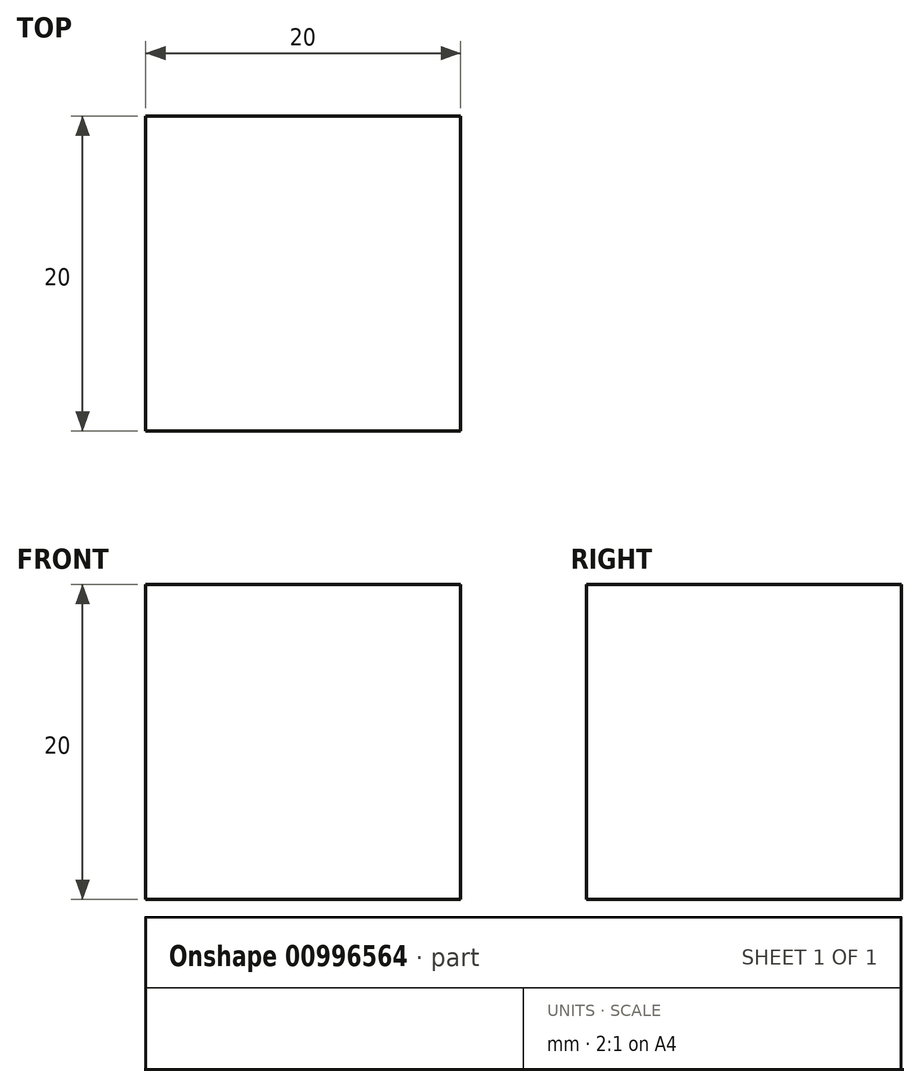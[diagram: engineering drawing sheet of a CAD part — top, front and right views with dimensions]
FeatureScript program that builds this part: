
annotation { "Feature Type Name" : "Feature", "Feature Type Description" : "" }
export const myFeature = defineFeature(function(context is Context, id is Id, definition is map)
    precondition{}
    {
        {
            var Q0;
            Q0=qCreatedBy(makeId("Top.planeOp"),FACE);
            var sketch = newSketch(context, id + "F0", { "sketchPlane" : qUnion([Q0])});
            skLineSegment(sketch, "E0.bottom", {"start": v(-20, 20) * mm, "end": v(0, 20) * mm});
            skLineSegment(sketch, "E0.top", {"start": v(-20, 0) * mm, "end": v(0, 0) * mm});
            skLineSegment(sketch, "E0.left", {"start": v(-20, 20) * mm, "end": v(-20, 0) * mm});
            skLineSegment(sketch, "E0.right", {"start": v(0, 20) * mm, "end": v(0, 0) * mm});
            skSolve(sketch);
        }
        {
            var Q0;
            Q0=makeQuery(id+"F0.imprint","IMPRINT",FACE,{"disambiguationData":[TD([[makeQuery(id+"F0.imprint","IMPRINT",EDGE,{"derivedFrom":sQuery(id+"F0.wireOp",EDGE,"E0.bottom")}),-1.0]])]});
            extrude(context, id + "F1", {"entities" : qUnion([Q0]), "depth" : 20 * mm, "offsetDistance" : 25 * mm});
        }
    });
